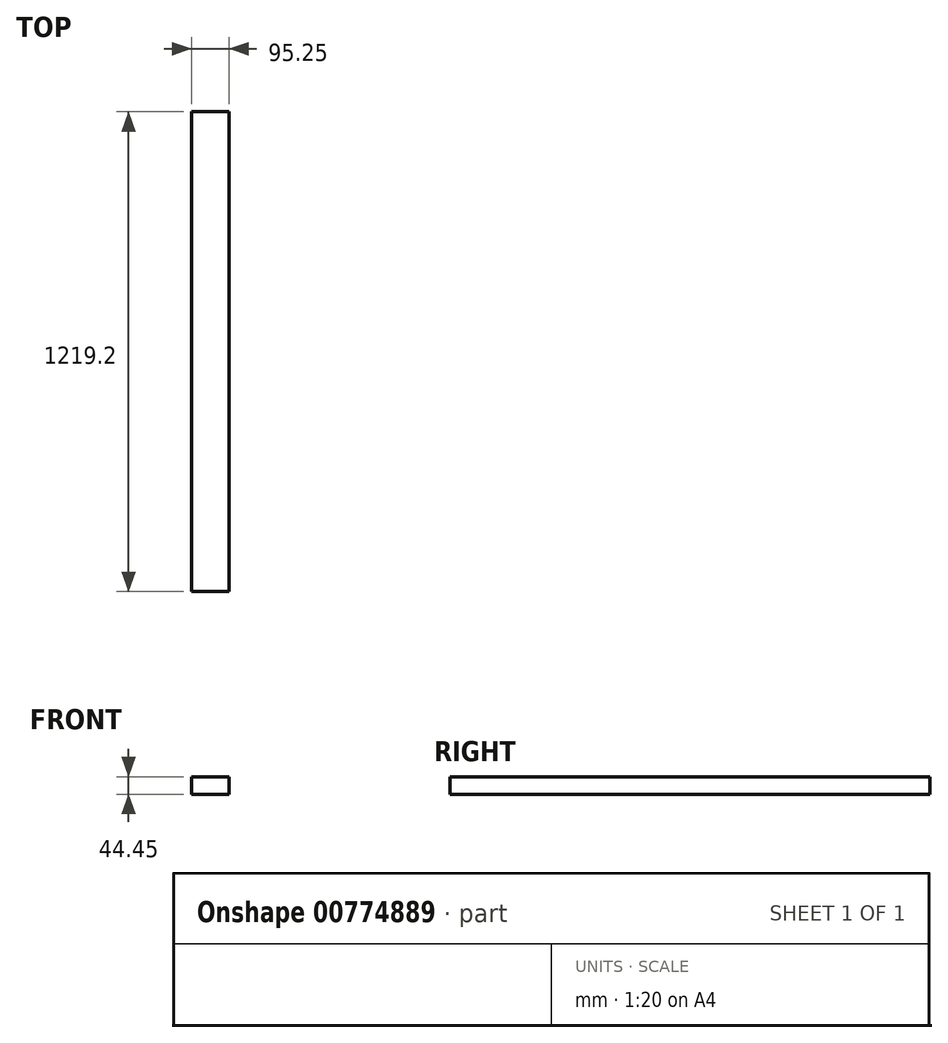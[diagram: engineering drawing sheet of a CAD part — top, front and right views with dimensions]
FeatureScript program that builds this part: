
annotation { "Feature Type Name" : "Feature", "Feature Type Description" : "" }
export const myFeature = defineFeature(function(context is Context, id is Id, definition is map)
    precondition{}
    {
        {
            var Q0;
            Q0=qCreatedBy(makeId("Front.planeOp"),FACE);
            var sketch = newSketch(context, id + "F0", { "sketchPlane" : qUnion([Q0])});
            skLineSegment(sketch, "E0.bottom", {"start": v(0, 0) * mm, "end": v(95.25, 0) * mm});
            skLineSegment(sketch, "E0.top", {"start": v(0, 44.45) * mm, "end": v(95.25, 44.45) * mm});
            skLineSegment(sketch, "E0.left", {"start": v(0, 0) * mm, "end": v(0, 44.45) * mm});
            skLineSegment(sketch, "E0.right", {"start": v(95.25, 0) * mm, "end": v(95.25, 44.45) * mm});
            skSolve(sketch);
        }
        {
            var Q0;
            Q0 = qSketchRegion(id + "F0", true);
            extrude(context, id + "F1", {"entities" : qUnion([Q0]), "depth" : 1219.2 * mm, "offsetDistance" : 25.4 * mm});
        }
    });
